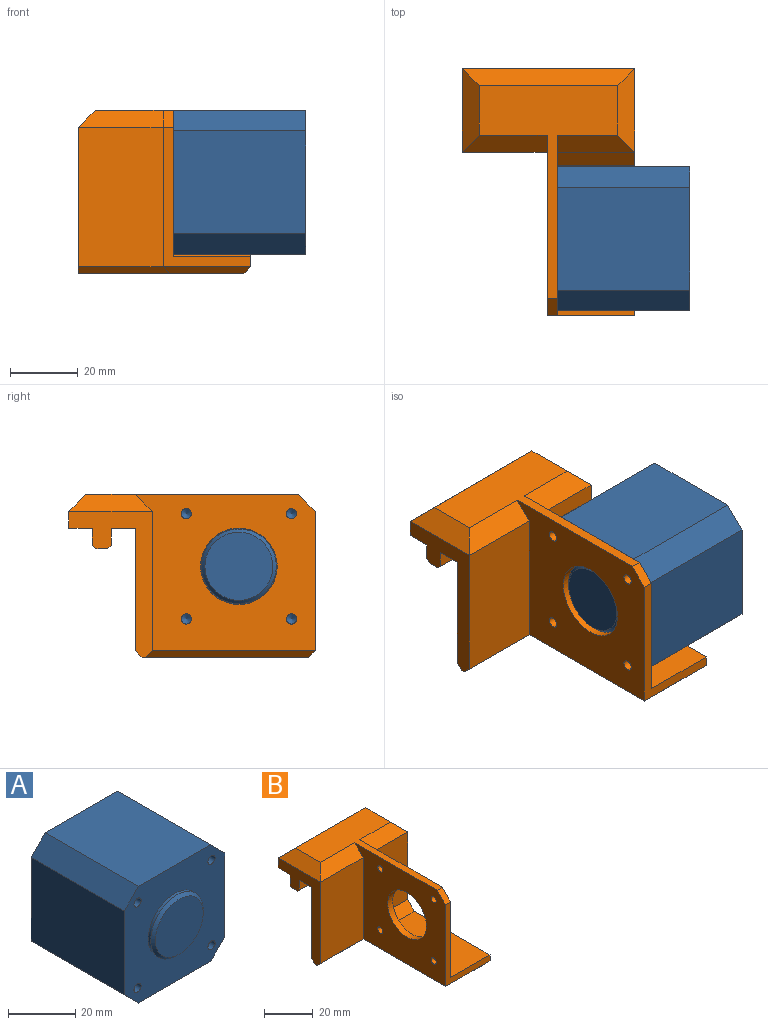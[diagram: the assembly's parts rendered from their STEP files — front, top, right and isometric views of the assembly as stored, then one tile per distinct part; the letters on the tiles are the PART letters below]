
ASSEMBLY  parts=2 mates=1
PART A: 21 faces, bbox 42.3x41x42.3 mm
  f0: plane 39x30.3mm, normal (0,0,1), area 1181.7mm2, adj f4,f5,f18,f20
  f1: plane 39x30.3mm, normal (-1,0,0), area 1181.7mm2, adj f4,f5,f19,f20
  f2: plane 39x30.3mm, normal (0,0,-1), area 1181.7mm2, adj f4,f5,f17,f19
  f3: plane 39x30.3mm, normal (1,0,0), area 1181.7mm2, adj f4,f5,f17,f18
  f4: plane 42.3x42.3mm, normal (0,-1,0), area 1308.9mm2, adj f0,f1,f2,f3,f6,f9,f11,f13
  f5: plane 42.3x42.3mm, normal (0,1,0), area 1717.3mm2, adj f0,f1,f2,f3,f17,f18,f19,f20
  f6: cylinder r=11mm len=22mm, axis (0,1,0), area 69.1mm2, adj f4,f8
  f7: plane 20x20mm, normal (0,-1,0), area 314.2mm2, adj f8
  f8: cone r=10mm half-angle=45deg, axis (0,1,0), area 93.3mm2, adj f6,f7
  f9: cylinder r=1.5mm len=10mm, axis (0,-1,0), area 94.2mm2, adj f4,f10
  f10: cone r=0mm half-angle=59deg, axis (0,-1,0), area 8.2mm2, adj f9
  f11: cylinder r=1.5mm len=10mm, axis (0,-1,0), area 94.2mm2, adj f4,f12
  f12: cone r=0mm half-angle=59deg, axis (0,-1,0), area 8.2mm2, adj f11
  f13: cylinder r=1.5mm len=10mm, axis (0,-1,0), area 94.2mm2, adj f4,f14
  f14: cone r=0mm half-angle=59deg, axis (0,-1,0), area 8.2mm2, adj f13
  f15: cylinder r=1.5mm len=10mm, axis (0,-1,0), area 94.2mm2, adj f4,f16
  f16: cone r=0mm half-angle=59deg, axis (0,-1,0), area 8.2mm2, adj f15
  f17: plane 39x6mm, normal (0.71,0,-0.71), area 330.9mm2, adj f2,f3,f4,f5
  f18: plane 39x6mm, normal (0.71,0,0.71), area 330.9mm2, adj f0,f3,f4,f5
  f19: plane 39x6mm, normal (-0.71,0,-0.71), area 330.9mm2, adj f1,f2,f4,f5
  f20: plane 39x6mm, normal (-0.71,0,0.71), area 330.9mm2, adj f0,f1,f4,f5
PART B: 36 faces, bbox 50.8x72.6x48 mm
  f0: plane 49x48.8mm, normal (0,0,-1), area 1095.2mm2, adj f5,f25,f26,f27,f28,f29
  f1: plane 41x25mm, normal (0,-1,0), area 1025mm2, adj f5,f15,f29,f30
  f2: plane 34x22.8mm, normal (0,-1,0), area 775.2mm2, adj f6,f14,f17,f34
  f3: plane 62.6x40.8mm, normal (0,0,1), area 739.7mm2, adj f14,f15,f30,f31,f32,f33,f34,f35
  f4: plane 50.8x7.1mm, normal (0,0,-1), area 360.7mm2, adj f5,f6,f9,f12
  f5: plane 43x24.6mm, normal (-1,0,0), area 341mm2, adj f0,f1,f4,f7,f8,f9,f10,f11
  f6: plane 72.6x41mm, normal (1,0,0), area 487mm2, adj f2,f4,f7,f8,f9,f10,f11,f12
  f7: plane 50.8x5mm, normal (0,1,0), area 254mm2, adj f5,f6,f8,f32
  f8: plane 50.8x7mm, normal (0,0,-1), area 355.6mm2, adj f5,f6,f7,f10
  f9: plane 50.8x5mm, normal (0,-1,0), area 254mm2, adj f4,f5,f6,f23
  f10: plane 50.8x5mm, normal (0,1,0), area 254mm2, adj f5,f6,f8,f24
  f11: plane 50.8x3.5mm, normal (0,0,-1), area 177.8mm2, adj f5,f6,f23,f24
  f12: plane 50.8x36mm, normal (0,1,0), area 1828.8mm2, adj f4,f5,f6,f25
  f13: plane 44x22.8mm, normal (0,0,1), area 1003.2mm2, adj f6,f14,f16,f17
  f14: plane 53x43mm, normal (1,0,0), area 1630.1mm2, adj f2,f3,f13,f16,f17,f18,f19,f20
  f15: plane 53x46mm, normal (-1,0,0), area 1782.1mm2, adj f1,f3,f16,f18,f19,f20,f21,f22
  f16: plane 41x25.8mm, normal (0,-1,0), area 191.4mm2, adj f6,f13,f14,f15,f27,f35
  f17: plane 22.8x4mm, normal (0,-0.71,0.71), area 129mm2, adj f2,f6,f13,f14
  f18: cylinder r=1.5mm len=3mm, axis (1,0,0), area 28.3mm2, adj f14,f15
  f19: cylinder r=1.5mm len=3mm, axis (1,0,0), area 28.3mm2, adj f14,f15
  f20: cylinder r=1.5mm len=3mm, axis (1,0,0), area 28.3mm2, adj f14,f15
  f21: cylinder r=1.5mm len=3mm, axis (1,0,0), area 28.3mm2, adj f14,f15
  f22: cylinder r=11.25mm len=22.5mm, axis (1,0,0), area 212.1mm2, adj f14,f15
  f23: plane 50.8x1mm, normal (0,-0.71,-0.71), area 71.8mm2, adj f5,f6,f9,f11
  f24: plane 50.8x1mm, normal (0,0.71,-0.71), area 71.8mm2, adj f5,f6,f10,f11
  f25: plane 50.8x2mm, normal (0,0.71,-0.71), area 140.9mm2, adj f0,f5,f12,f26
  f26: plane 53x2mm, normal (0.71,0,-0.71), area 144.2mm2, adj f0,f6,f25,f27
  f27: plane 25.8x2mm, normal (0,-0.71,-0.71), area 67.3mm2, adj f0,f16,f26,f28
  f28: plane 50x2mm, normal (-0.71,0,-0.71), area 135.8mm2, adj f0,f15,f27,f29
  f29: plane 27x2mm, normal (0,-0.71,-0.71), area 73.5mm2, adj f0,f1,f5,f28
  f30: plane 25x5mm, normal (0,-0.71,0.71), area 159.1mm2, adj f1,f3,f15,f31
  f31: plane 24.6x5mm, normal (-0.71,0,0.71), area 138.6mm2, adj f3,f5,f30,f32
  f32: plane 50.8x5mm, normal (0,0.71,0.71), area 323.9mm2, adj f3,f7,f31,f33
  f33: plane 24.6x5mm, normal (0.71,0,0.71), area 138.6mm2, adj f3,f6,f32,f34
  f34: plane 22.8x5mm, normal (0,-0.71,0.71), area 143.5mm2, adj f2,f3,f14,f33
  f35: plane 5x5mm, normal (0,-0.71,0.71), area 21.2mm2, adj f3,f14,f15,f16
PLACE A rot(axis=(0,0,-1),90deg) t=(42.32,-9.59,-32.3)mm
PLACE B at identity
MATE fastened A.f6 <-> B.f22  axis (-1,0,0) through (3.32,-30.74,-11.15)mm
